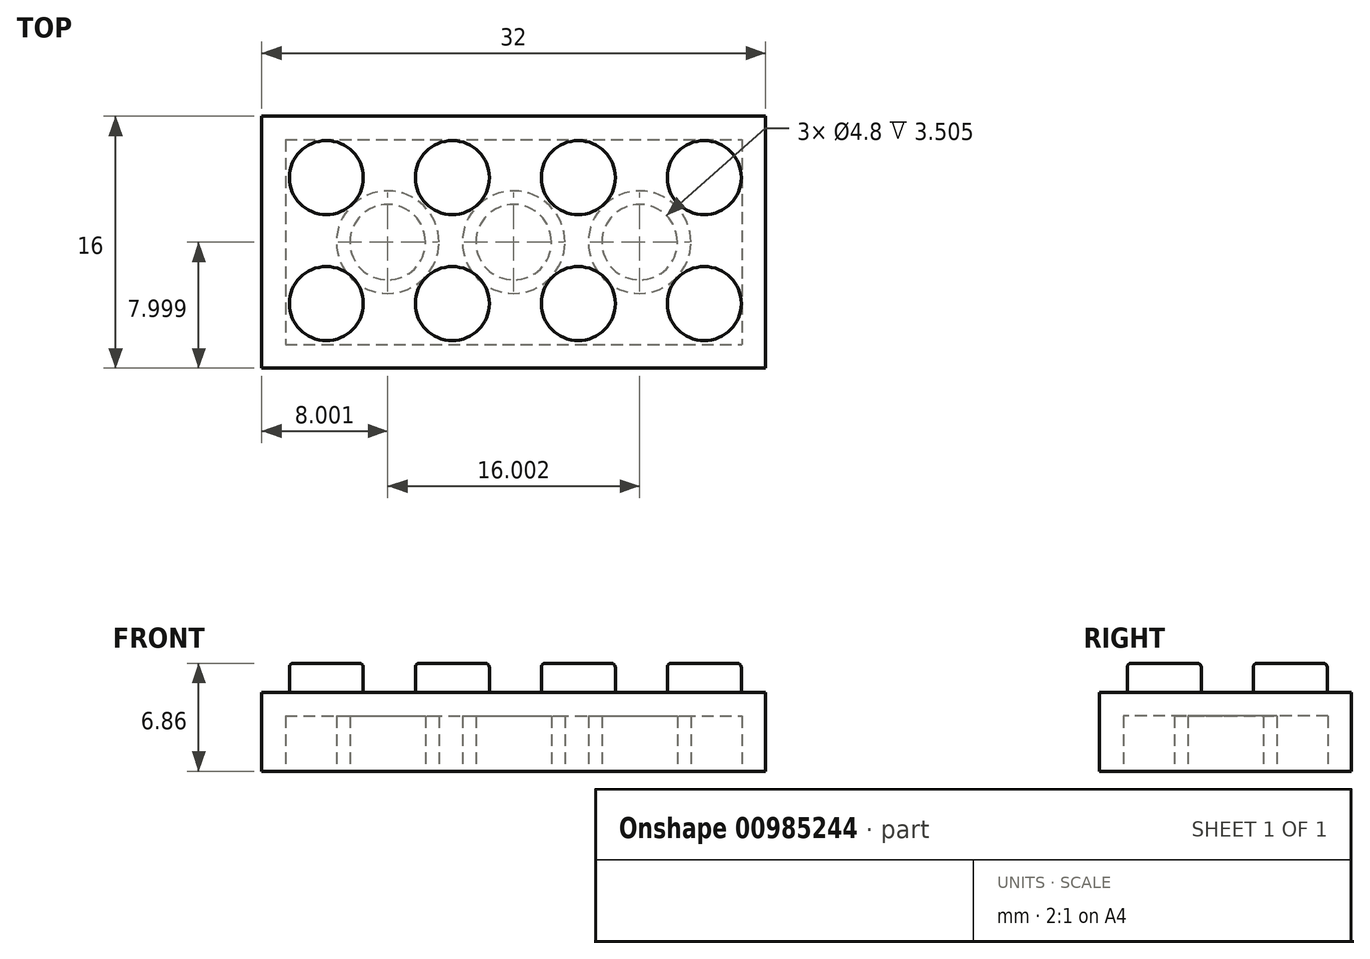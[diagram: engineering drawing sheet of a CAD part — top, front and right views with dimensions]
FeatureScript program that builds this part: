
annotation { "Feature Type Name" : "Feature", "Feature Type Description" : "" }
export const myFeature = defineFeature(function(context is Context, id is Id, definition is map)
    precondition{}
    {
        {
            var Q0;
            Q0=qCreatedBy(makeId("Top.planeOp"),FACE);
            var sketch = newSketch(context, id + "F0", { "sketchPlane" : qUnion([Q0])});
            skLineSegment(sketch, "E0.bottom", {"start": v(0, 0) * mm, "end": v(32, 0) * mm});
            skLineSegment(sketch, "E0.top", {"start": v(0, -16) * mm, "end": v(32, -16) * mm});
            skLineSegment(sketch, "E0.left", {"start": v(0, 0) * mm, "end": v(0, -16) * mm});
            skLineSegment(sketch, "E0.right", {"start": v(32, 0) * mm, "end": v(32, -16) * mm});
            skSolve(sketch);
        }
        {
            var Q0;
            Q0=makeQuery(id+"F0.imprint","IMPRINT",FACE,{"disambiguationData":[TD([[makeQuery(id+"F0.imprint","IMPRINT",EDGE,{"derivedFrom":sQuery(id+"F0.wireOp",EDGE,"E0.bottom")}),-1.0]])]});
            extrude(context, id + "F1", {"entities" : qUnion([Q0]), "depth" : 5 * mm, "offsetDistance" : 25.4 * mm});
        }
        {
            var Q0;
            Q0=makeQuery(id+"F1.opExtrude","CAP_FACE",FACE,{"disambiguationData":[OSD([sQuery(id+"F0.wireOp",EDGE,"E0.bottom"),sQuery(id+"F0.wireOp",EDGE,"E0.top"),sQuery(id+"F0.wireOp",EDGE,"E0.left"),sQuery(id+"F0.wireOp",EDGE,"E0.right")])],"isStart":false});
            var sketch = newSketch(context, id + "F2", { "sketchPlane" : qUnion([Q0])});
            skCircle(sketch, "E1", {"center": v(28.1, -3.9) * mm, "radius": 2.35 * mm});
            skCircle(sketch, "E2.0.1.0", {"center": v(28.1, -11.9) * mm, "radius": 2.35 * mm});
            skCircle(sketch, "E2.1.0.0", {"center": v(20.1, -3.9) * mm, "radius": 2.35 * mm});
            skCircle(sketch, "E2.1.1.0", {"center": v(20.1, -11.9) * mm, "radius": 2.35 * mm});
            skCircle(sketch, "E2.2.0.0", {"center": v(12.1, -3.9) * mm, "radius": 2.35 * mm});
            skCircle(sketch, "E2.2.1.0", {"center": v(12.1, -11.9) * mm, "radius": 2.35 * mm});
            skCircle(sketch, "E2.3.0.0", {"center": v(4.1, -3.9) * mm, "radius": 2.35 * mm});
            skCircle(sketch, "E2.3.1.0", {"center": v(4.1, -11.9) * mm, "radius": 2.35 * mm});
            skLineSegment(sketch, "E2.direction1", {"start": v(28.1, -3.9) * mm, "end": v(20.1, -3.9) * mm, "construction": true});
            skLineSegment(sketch, "E2.direction2", {"start": v(28.1, -3.9) * mm, "end": v(28.1, -11.9) * mm, "construction": true});
            skSolve(sketch);
        }
        {
            var Q0;
            Q0=makeQuery(id+"F2.imprint","IMPRINT",FACE,{"disambiguationData":[TD([[makeQuery(id+"F2.imprint","IMPRINT",EDGE,{"derivedFrom":sQuery(id+"F2.wireOp",EDGE,"E1")}),1.0]])]});
            var Q1;
            Q1=makeQuery(id+"F2.imprint","IMPRINT",FACE,{"disambiguationData":[TD([[makeQuery(id+"F2.imprint","IMPRINT",EDGE,{"derivedFrom":sQuery(id+"F2.wireOp",EDGE,"E2.0.1.0")}),1.0]])]});
            var Q2;
            Q2=makeQuery(id+"F2.imprint","IMPRINT",FACE,{"disambiguationData":[TD([[makeQuery(id+"F2.imprint","IMPRINT",EDGE,{"derivedFrom":sQuery(id+"F2.wireOp",EDGE,"E2.1.1.0")}),1.0]])]});
            var Q3;
            Q3=makeQuery(id+"F2.imprint","IMPRINT",FACE,{"disambiguationData":[TD([[makeQuery(id+"F2.imprint","IMPRINT",EDGE,{"derivedFrom":sQuery(id+"F2.wireOp",EDGE,"E2.1.0.0")}),1.0]])]});
            var Q4;
            Q4=makeQuery(id+"F2.imprint","IMPRINT",FACE,{"disambiguationData":[TD([[makeQuery(id+"F2.imprint","IMPRINT",EDGE,{"derivedFrom":sQuery(id+"F2.wireOp",EDGE,"E2.2.0.0")}),1.0]])]});
            var Q5;
            Q5=makeQuery(id+"F2.imprint","IMPRINT",FACE,{"disambiguationData":[TD([[makeQuery(id+"F2.imprint","IMPRINT",EDGE,{"derivedFrom":sQuery(id+"F2.wireOp",EDGE,"E2.2.1.0")}),1.0]])]});
            var Q6;
            Q6=makeQuery(id+"F2.imprint","IMPRINT",FACE,{"disambiguationData":[TD([[makeQuery(id+"F2.imprint","IMPRINT",EDGE,{"derivedFrom":sQuery(id+"F2.wireOp",EDGE,"E2.3.1.0")}),1.0]])]});
            var Q7;
            Q7=makeQuery(id+"F2.imprint","IMPRINT",FACE,{"disambiguationData":[TD([[makeQuery(id+"F2.imprint","IMPRINT",EDGE,{"derivedFrom":sQuery(id+"F2.wireOp",EDGE,"E2.3.0.0")}),1.0]])]});
            extrude(context, id + "F3", {"entities" : qUnion([Q0, Q1, Q2, Q3, Q4, Q5, Q6, Q7]), "operationType" : NewBodyOperationType.ADD, "depth" : 1.85 * mm, "offsetDistance" : 25.4 * mm});
        }
        {
            var Q0;
            Q0=makeQuery(id+"F3.opExtrude","CAP_EDGE",EDGE,{"disambiguationData":[OSD([sQuery(id+"F2.wireOp",EDGE,"E1")])],"isStart":false});
            var Q1;
            Q1=makeQuery(id+"F3.opExtrude","CAP_EDGE",EDGE,{"disambiguationData":[OSD([sQuery(id+"F2.wireOp",EDGE,"E2.0.1.0")])],"isStart":false});
            var Q2;
            Q2=makeQuery(id+"F3.opExtrude","CAP_EDGE",EDGE,{"disambiguationData":[OSD([sQuery(id+"F2.wireOp",EDGE,"E2.1.1.0")])],"isStart":false});
            var Q3;
            Q3=makeQuery(id+"F3.opExtrude","CAP_EDGE",EDGE,{"disambiguationData":[OSD([sQuery(id+"F2.wireOp",EDGE,"E2.1.0.0")])],"isStart":false});
            var Q4;
            Q4=makeQuery(id+"F3.opExtrude","CAP_EDGE",EDGE,{"disambiguationData":[OSD([sQuery(id+"F2.wireOp",EDGE,"E2.2.0.0")])],"isStart":false});
            var Q5;
            Q5=makeQuery(id+"F3.opExtrude","CAP_EDGE",EDGE,{"disambiguationData":[OSD([sQuery(id+"F2.wireOp",EDGE,"E2.2.1.0")])],"isStart":false});
            var Q6;
            Q6=makeQuery(id+"F3.opExtrude","CAP_EDGE",EDGE,{"disambiguationData":[OSD([sQuery(id+"F2.wireOp",EDGE,"E2.3.1.0")])],"isStart":false});
            var Q7;
            Q7=makeQuery(id+"F3.opExtrude","CAP_EDGE",EDGE,{"disambiguationData":[OSD([sQuery(id+"F2.wireOp",EDGE,"E2.3.0.0")])],"isStart":false});
            fillet(context, id + "F4", {"entities" : qUnion([Q0, Q1, Q2, Q3, Q4, Q5, Q6, Q7]), "radius" : 0.25 * mm, "tangentPropagation" : true, "allowEdgeOverflow" : false});
        }
        {
            var Q0;
            Q0=makeQuery(id+"F1.opExtrude","CAP_FACE",FACE,{"disambiguationData":[OSD([sQuery(id+"F0.wireOp",EDGE,"E0.bottom"),sQuery(id+"F0.wireOp",EDGE,"E0.top"),sQuery(id+"F0.wireOp",EDGE,"E0.left"),sQuery(id+"F0.wireOp",EDGE,"E0.right")])],"isStart":true});
            var sketch = newSketch(context, id + "F5", { "sketchPlane" : qUnion([Q0])});
            skLineSegment(sketch, "E3.0", {"start": v(1.5, 1.5) * mm, "end": v(30.5, 1.5) * mm});
            skLineSegment(sketch, "E3.1", {"start": v(1.5, 1.5) * mm, "end": v(1.5, 14.5) * mm});
            skLineSegment(sketch, "E3.2", {"start": v(1.5, 14.5) * mm, "end": v(30.5, 14.5) * mm});
            skLineSegment(sketch, "E3.3", {"start": v(30.5, 1.5) * mm, "end": v(30.5, 14.5) * mm});
            skLineSegment(sketch, "E4", {"start": v(32, 0) * mm, "end": v(0, 16) * mm});
            skLineSegment(sketch, "E5", {"start": v(0, 16) * mm, "end": v(0, 0) * mm});
            skLineSegment(sketch, "E6", {"start": v(0, 0) * mm, "end": v(32, 16) * mm});
            skCircle(sketch, "E7", {"center": v(16, 8) * mm, "radius": 3.25 * mm});
            skCircle(sketch, "E8", {"center": v(16, 8) * mm, "radius": 2.4 * mm});
            skCircle(sketch, "E9", {"center": v(24, 8) * mm, "radius": 2.4 * mm});
            skCircle(sketch, "E10", {"center": v(24, 8) * mm, "radius": 3.25 * mm});
            skCircle(sketch, "E11", {"center": v(8, 8) * mm, "radius": 2.4 * mm});
            skCircle(sketch, "E12", {"center": v(8, 8) * mm, "radius": 3.25 * mm});
            skSolve(sketch);
        }
        {
            var Q0;
            {var subQ0=sQuery(id+"F5.wireOp",EDGE,"E4");var subQ1=sQuery(id+"F5.wireOp",EDGE,"E3.2");var subQ2=makeQuery(id+"F5.imprint","INTERSECT",VERTEX,{"derivedFrom":[subQ1,subQ0]});Q0=makeQuery(id+"F5.imprint","IMPRINT",FACE,{"disambiguationData":[TD([[makeQuery(id+"F5.imprint","IMPRINT",EDGE,{"disambiguationData":[TD([[subQ2,-1.0]])],"derivedFrom":subQ1}),-1.0]])]});}
            var Q1;
            {var subQ5=sQuery(id+"F5.wireOp",EDGE,"E3.1");Q1=makeQuery(id+"F5.imprint","IMPRINT",FACE,{"disambiguationData":[TD([[makeQuery(id+"F5.imprint","IMPRINT",EDGE,{"derivedFrom":subQ5}),-1.0]])]});}
            var Q2;
            {var subQ5=sQuery(id+"F5.wireOp",EDGE,"E3.3");Q2=makeQuery(id+"F5.imprint","IMPRINT",FACE,{"disambiguationData":[TD([[makeQuery(id+"F5.imprint","IMPRINT",EDGE,{"derivedFrom":subQ5}),1.0]])]});}
            var Q3;
            Q3=makeQuery(id+"F5.imprint","IMPRINT",FACE,{"disambiguationData":[TD([[makeQuery(id+"F5.imprint","IMPRINT",EDGE,{"derivedFrom":sQuery(id+"F5.wireOp",EDGE,"E9")}),1.0]])]});
            var Q4;
            {var subQ0=sQuery(id+"F5.wireOp",EDGE,"E6");var subQ1=sQuery(id+"F5.wireOp",EDGE,"E3.0");var subQ2=makeQuery(id+"F5.imprint","INTERSECT",VERTEX,{"derivedFrom":[subQ1,subQ0]});Q4=makeQuery(id+"F5.imprint","IMPRINT",FACE,{"disambiguationData":[TD([[makeQuery(id+"F5.imprint","IMPRINT",EDGE,{"disambiguationData":[TD([[subQ2,-1.0]])],"derivedFrom":subQ1}),1.0]])]});}
            var Q5;
            {var subQ0=sQuery(id+"F5.wireOp",EDGE,"E6");var subQ1=sQuery(id+"F5.wireOp",EDGE,"E4");var subQ2=makeQuery(id+"F5.imprint","INTERSECT",VERTEX,{"derivedFrom":[subQ1,subQ0]});Q5=makeQuery(id+"F5.imprint","IMPRINT",FACE,{"disambiguationData":[TD([[makeQuery(id+"F5.imprint","IMPRINT",EDGE,{"disambiguationData":[TD([[subQ2,-1.0]])],"derivedFrom":subQ1}),-1.0]])]});}
            var Q6;
            {var subQ0=sQuery(id+"F5.wireOp",EDGE,"E8");var subQ1=sQuery(id+"F5.wireOp",EDGE,"E4");var subQ2=makeQuery(id+"F5.imprint","INTERSECT",VERTEX,{"disambiguationData":[OD(0.0)],"derivedFrom":[subQ1,subQ0]});Q6=makeQuery(id+"F5.imprint","IMPRINT",FACE,{"disambiguationData":[TD([[makeQuery(id+"F5.imprint","IMPRINT",EDGE,{"disambiguationData":[TD([[subQ2,-1.0]])],"derivedFrom":subQ1}),-1.0]])]});}
            var Q7;
            {var subQ0=sQuery(id+"F5.wireOp",EDGE,"E8");var subQ1=sQuery(id+"F5.wireOp",EDGE,"E4");var subQ2=makeQuery(id+"F5.imprint","INTERSECT",VERTEX,{"disambiguationData":[OD(0.0)],"derivedFrom":[subQ1,subQ0]});Q7=makeQuery(id+"F5.imprint","IMPRINT",FACE,{"disambiguationData":[TD([[makeQuery(id+"F5.imprint","IMPRINT",EDGE,{"disambiguationData":[TD([[subQ2,-1.0]])],"derivedFrom":subQ1}),1.0]])]});}
            var Q8;
            {var subQ0=sQuery(id+"F5.wireOp",EDGE,"E6");var subQ1=sQuery(id+"F5.wireOp",EDGE,"E4");var subQ2=makeQuery(id+"F5.imprint","INTERSECT",VERTEX,{"derivedFrom":[subQ1,subQ0]});Q8=makeQuery(id+"F5.imprint","IMPRINT",FACE,{"disambiguationData":[TD([[makeQuery(id+"F5.imprint","IMPRINT",EDGE,{"disambiguationData":[TD([[subQ2,-1.0]])],"derivedFrom":subQ1}),1.0]])]});}
            var Q9;
            Q9=makeQuery(id+"F5.imprint","IMPRINT",FACE,{"disambiguationData":[TD([[makeQuery(id+"F5.imprint","IMPRINT",EDGE,{"derivedFrom":sQuery(id+"F5.wireOp",EDGE,"E11")}),1.0]])]});
            var Q10;
            Q10=makeQuery(id+"F1.opExtrude","CAP_FACE",FACE,{"disambiguationData":[OSD([sQuery(id+"F0.wireOp",EDGE,"E0.bottom"),sQuery(id+"F0.wireOp",EDGE,"E0.top"),sQuery(id+"F0.wireOp",EDGE,"E0.left"),sQuery(id+"F0.wireOp",EDGE,"E0.right")])],"isStart":false});
            extrude(context, id + "F6", {"entities" : qUnion([Q0, Q1, Q2, Q3, Q4, Q5, Q6, Q7, Q8, Q9, Q10]), "operationType" : NewBodyOperationType.REMOVE, "oppositeDirection" : true, "depth" : 3.5 * mm, "offsetDistance" : 25.4 * mm});
        }
    });
